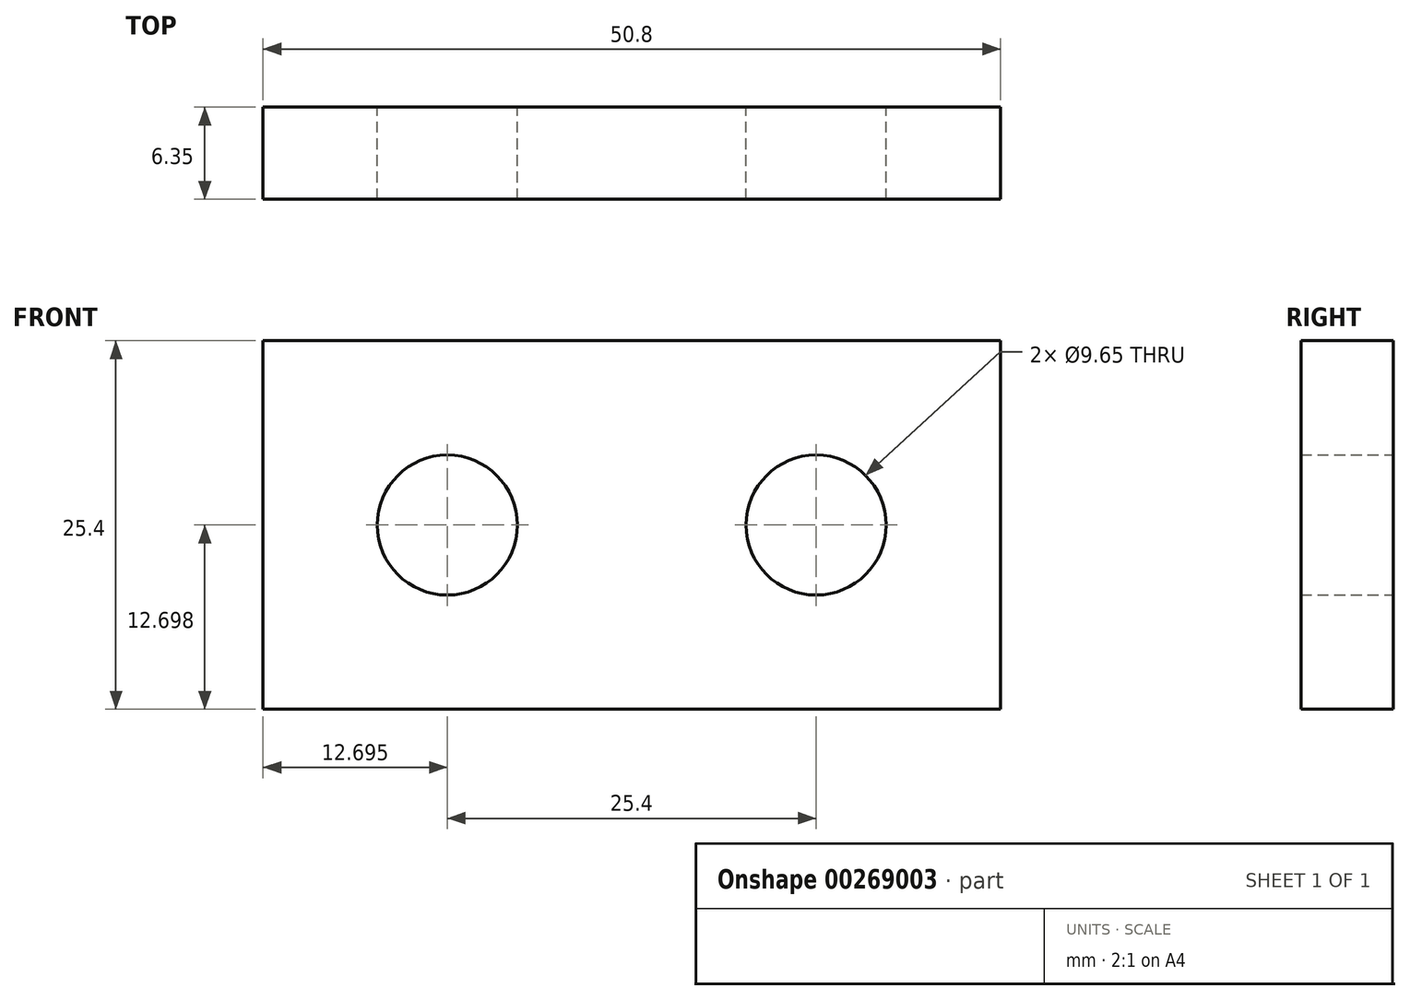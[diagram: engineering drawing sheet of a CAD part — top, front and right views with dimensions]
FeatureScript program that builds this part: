
annotation { "Feature Type Name" : "Feature", "Feature Type Description" : "" }
export const myFeature = defineFeature(function(context is Context, id is Id, definition is map)
    precondition{}
    {
        {
            var Q0;
            Q0=qCreatedBy(makeId("Front.planeOp"),FACE);
            var sketch = newSketch(context, id + "F0", { "sketchPlane" : qUnion([Q0])});
            skLineSegment(sketch, "E0.bottom", {"start": v(-101.4, 24.92) * mm, "end": v(-50.6, 24.92) * mm});
            skLineSegment(sketch, "E0.top", {"start": v(-101.4, -0.48) * mm, "end": v(-50.6, -0.48) * mm});
            skLineSegment(sketch, "E0.left", {"start": v(-101.4, 24.92) * mm, "end": v(-101.4, -0.48) * mm});
            skLineSegment(sketch, "E0.right", {"start": v(-50.6, 24.92) * mm, "end": v(-50.6, -0.48) * mm});
            skLineSegment(sketch, "E1", {"start": v(-101.4, 12.22) * mm, "end": v(-76, 12.22) * mm, "construction": true});
            skPoint(sketch, "E1.endSnap0", {"position": v(-76, 24.92) * mm});
            skLineSegment(sketch, "E2", {"start": v(-76, 12.22) * mm, "end": v(-50.6, 12.22) * mm, "construction": true});
            skCircle(sketch, "E3", {"center": v(-88.7, 12.22) * mm, "radius": 4.83 * mm});
            skCircle(sketch, "E4", {"center": v(-63.3, 12.22) * mm, "radius": 4.83 * mm});
            skSolve(sketch);
        }
        {
            var Q0;
            Q0 = qSketchRegion(id + "F0", true);
            extrude(context, id + "F1", {"entities" : qUnion([Q0]), "depth" : 6.35 * mm});
        }
    });
